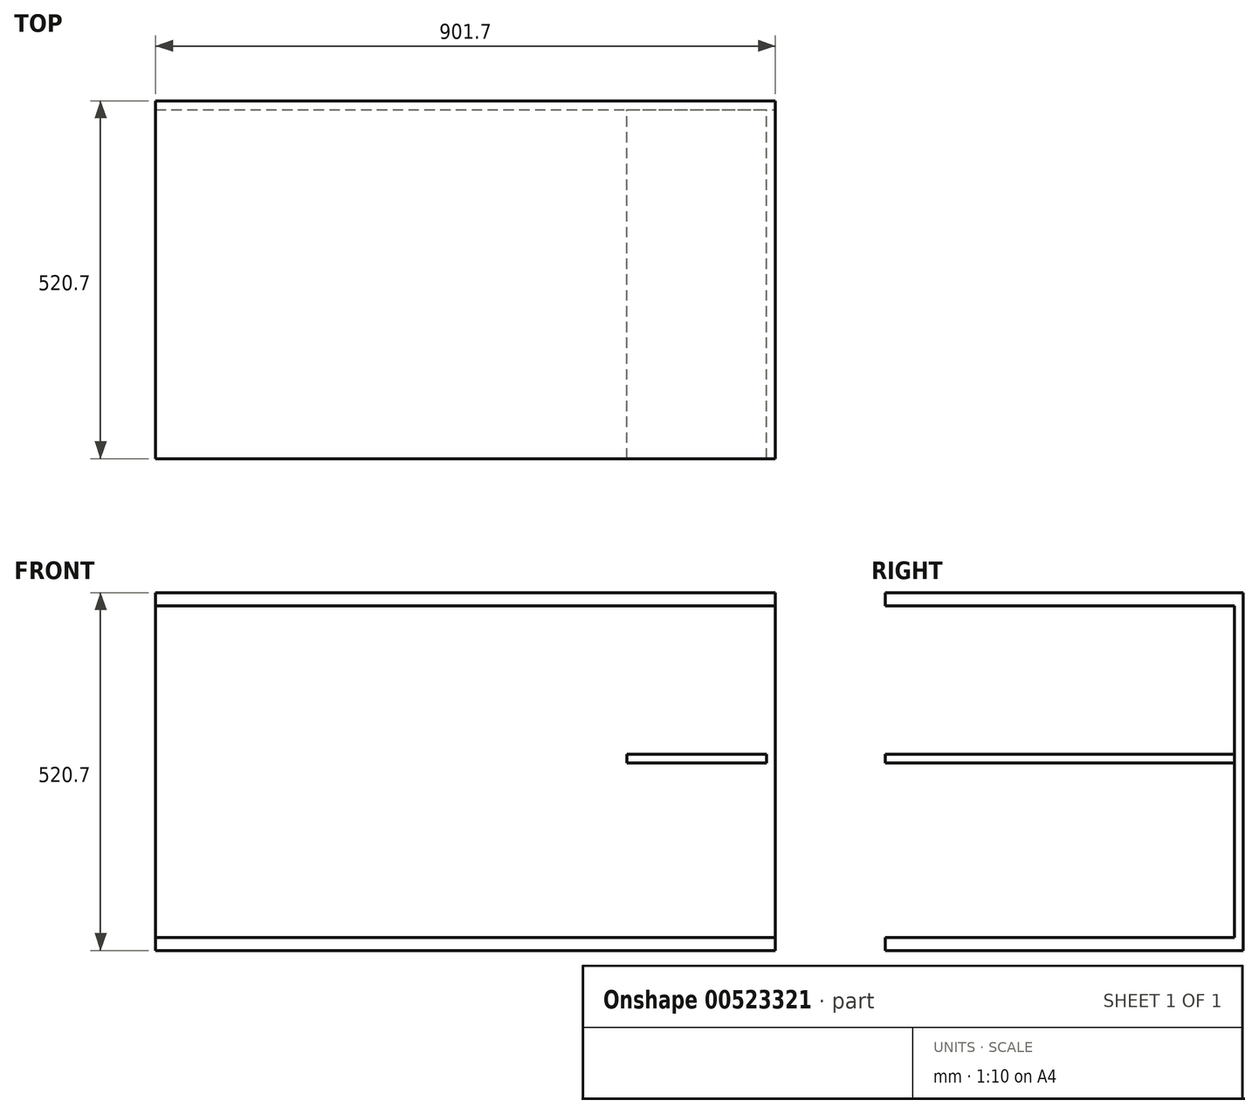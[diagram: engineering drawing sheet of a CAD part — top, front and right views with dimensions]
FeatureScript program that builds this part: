
annotation { "Feature Type Name" : "Feature", "Feature Type Description" : "" }
export const myFeature = defineFeature(function(context is Context, id is Id, definition is map)
    precondition{}
    {
        {
            var Q0;
            Q0=qCreatedBy(makeId("Front.planeOp"),FACE);
            var sketch = newSketch(context, id + "F0", { "sketchPlane" : qUnion([Q0])});
            skLineSegment(sketch, "E0.bottom", {"start": v(-12.7, 82.55) * mm, "end": v(889, 82.55) * mm});
            skLineSegment(sketch, "E0.top", {"start": v(-12.7, 63.5) * mm, "end": v(889, 63.5) * mm});
            skLineSegment(sketch, "E0.left", {"start": v(-12.7, 82.55) * mm, "end": v(-12.7, 63.5) * mm});
            skLineSegment(sketch, "E0.right", {"start": v(889, 82.55) * mm, "end": v(889, 63.5) * mm});
            skLineSegment(sketch, "E1.bottom", {"start": v(-12.7, 82.55) * mm, "end": v(0, 82.55) * mm});
            skLineSegment(sketch, "E1.top", {"start": v(-12.7, 565.15) * mm, "end": v(0, 565.15) * mm});
            skLineSegment(sketch, "E1.left", {"start": v(-12.7, 82.55) * mm, "end": v(-12.7, 565.15) * mm});
            skLineSegment(sketch, "E1.right", {"start": v(0, 82.55) * mm, "end": v(0, 565.15) * mm});
            skLineSegment(sketch, "E2.bottom", {"start": v(-12.7, 565.15) * mm, "end": v(889, 565.15) * mm});
            skLineSegment(sketch, "E2.top", {"start": v(-12.7, 584.2) * mm, "end": v(889, 584.2) * mm});
            skLineSegment(sketch, "E2.left", {"start": v(-12.7, 565.15) * mm, "end": v(-12.7, 584.2) * mm});
            skLineSegment(sketch, "E2.right", {"start": v(889, 565.15) * mm, "end": v(889, 584.2) * mm});
            skLineSegment(sketch, "E3.bottom", {"start": v(889, 82.55) * mm, "end": v(876.3, 82.55) * mm});
            skLineSegment(sketch, "E3.top", {"start": v(889, 565.15) * mm, "end": v(876.3, 565.15) * mm});
            skLineSegment(sketch, "E3.left", {"start": v(889, 82.55) * mm, "end": v(889, 565.15) * mm});
            skLineSegment(sketch, "E3.right", {"start": v(876.3, 82.55) * mm, "end": v(876.3, 565.15) * mm});
            skLineSegment(sketch, "E4.bottom", {"start": v(133.35, 400.05) * mm, "end": v(146.05, 400.05) * mm});
            skLineSegment(sketch, "E4.top", {"start": v(133.35, 82.55) * mm, "end": v(146.05, 82.55) * mm});
            skLineSegment(sketch, "E4.left", {"start": v(133.35, 400.05) * mm, "end": v(133.35, 82.55) * mm});
            skLineSegment(sketch, "E4.right", {"start": v(146.05, 400.05) * mm, "end": v(146.05, 82.55) * mm});
            skLineSegment(sketch, "E5.bottom", {"start": v(241.3, 400.05) * mm, "end": v(254, 400.05) * mm});
            skLineSegment(sketch, "E5.top", {"start": v(241.3, 82.55) * mm, "end": v(254, 82.55) * mm});
            skLineSegment(sketch, "E5.left", {"start": v(241.3, 400.05) * mm, "end": v(241.3, 82.55) * mm});
            skLineSegment(sketch, "E5.right", {"start": v(254, 400.05) * mm, "end": v(254, 82.55) * mm});
            skLineSegment(sketch, "E6.bottom", {"start": v(412.75, 400.05) * mm, "end": v(425.45, 400.05) * mm});
            skLineSegment(sketch, "E6.top", {"start": v(412.75, 82.55) * mm, "end": v(425.45, 82.55) * mm});
            skLineSegment(sketch, "E6.left", {"start": v(412.75, 400.05) * mm, "end": v(412.75, 82.55) * mm});
            skLineSegment(sketch, "E6.right", {"start": v(425.45, 400.05) * mm, "end": v(425.45, 82.55) * mm});
            skLineSegment(sketch, "E7.bottom", {"start": v(539.75, 400.05) * mm, "end": v(552.45, 400.05) * mm});
            skLineSegment(sketch, "E7.top", {"start": v(539.75, 82.55) * mm, "end": v(552.45, 82.55) * mm});
            skLineSegment(sketch, "E7.left", {"start": v(539.75, 400.05) * mm, "end": v(539.75, 82.55) * mm});
            skLineSegment(sketch, "E7.right", {"start": v(552.45, 400.05) * mm, "end": v(552.45, 82.55) * mm});
            skLineSegment(sketch, "E8.bottom", {"start": v(660.4, 82.55) * mm, "end": v(673.1, 82.55) * mm});
            skLineSegment(sketch, "E8.top", {"start": v(660.4, 400.05) * mm, "end": v(673.1, 400.05) * mm});
            skLineSegment(sketch, "E8.left", {"start": v(660.4, 82.55) * mm, "end": v(660.4, 400.05) * mm});
            skLineSegment(sketch, "E8.right", {"start": v(673.1, 82.55) * mm, "end": v(673.1, 400.05) * mm});
            skLineSegment(sketch, "E9.bottom", {"start": v(0, 400.05) * mm, "end": v(673.1, 400.05) * mm});
            skLineSegment(sketch, "E9.top", {"start": v(0, 412.75) * mm, "end": v(673.1, 412.75) * mm});
            skLineSegment(sketch, "E9.left", {"start": v(0, 400.05) * mm, "end": v(0, 412.75) * mm});
            skLineSegment(sketch, "E9.right", {"start": v(673.1, 400.05) * mm, "end": v(673.1, 412.75) * mm});
            skLineSegment(sketch, "E10.bottom", {"start": v(673.1, 349.25) * mm, "end": v(876.3, 349.25) * mm});
            skLineSegment(sketch, "E10.top", {"start": v(673.1, 336.55) * mm, "end": v(876.3, 336.55) * mm});
            skLineSegment(sketch, "E10.left", {"start": v(673.1, 349.25) * mm, "end": v(673.1, 336.55) * mm});
            skLineSegment(sketch, "E10.right", {"start": v(876.3, 349.25) * mm, "end": v(876.3, 336.55) * mm});
            skLineSegment(sketch, "E11.bottom", {"start": v(673.1, 412.75) * mm, "end": v(660.4, 412.75) * mm});
            skLineSegment(sketch, "E11.top", {"start": v(673.1, 565.15) * mm, "end": v(660.4, 565.15) * mm});
            skLineSegment(sketch, "E11.left", {"start": v(673.1, 412.75) * mm, "end": v(673.1, 565.15) * mm});
            skLineSegment(sketch, "E11.right", {"start": v(660.4, 412.75) * mm, "end": v(660.4, 565.15) * mm});
            skLineSegment(sketch, "E12.bottom", {"start": v(457.2, 565.15) * mm, "end": v(469.9, 565.15) * mm});
            skLineSegment(sketch, "E12.top", {"start": v(457.2, 412.75) * mm, "end": v(469.9, 412.75) * mm});
            skLineSegment(sketch, "E12.left", {"start": v(457.2, 565.15) * mm, "end": v(457.2, 412.75) * mm});
            skLineSegment(sketch, "E12.right", {"start": v(469.9, 565.15) * mm, "end": v(469.9, 412.75) * mm});
            skLineSegment(sketch, "E13.bottom", {"start": v(241.3, 565.15) * mm, "end": v(254, 565.15) * mm});
            skLineSegment(sketch, "E13.top", {"start": v(241.3, 412.75) * mm, "end": v(254, 412.75) * mm});
            skLineSegment(sketch, "E13.left", {"start": v(241.3, 565.15) * mm, "end": v(241.3, 412.75) * mm});
            skLineSegment(sketch, "E13.right", {"start": v(254, 565.15) * mm, "end": v(254, 412.75) * mm});
            skSolve(sketch);
        }
        {
            var Q0;
            Q0=makeQuery(id+"F0.imprint","IMPRINT",FACE,{"disambiguationData":[TD([[makeQuery(id+"F0.imprint","IMPRINT",EDGE,{"derivedFrom":sQuery(id+"F0.wireOp",EDGE,"E2.top")}),-1.0]])]});
            var Q1;
            Q1=makeQuery(id+"F0.imprint","IMPRINT",FACE,{"disambiguationData":[TD([[makeQuery(id+"F0.imprint","IMPRINT",EDGE,{"derivedFrom":sQuery(id+"F0.wireOp",EDGE,"E13.bottom")}),-1.0]])]});
            var Q2;
            {var subQ4=sQuery(id+"F0.wireOp",EDGE,"E1.bottom");Q2=makeQuery(id+"F0.imprint","IMPRINT",FACE,{"disambiguationData":[TD([[makeQuery(id+"F0.imprint","IMPRINT",EDGE,{"derivedFrom":subQ4}),1.0]])]});}
            var Q3;
            {var subQ10=sQuery(id+"F0.wireOp",EDGE,"E9.left");Q3=makeQuery(id+"F0.imprint","IMPRINT",FACE,{"disambiguationData":[TD([[makeQuery(id+"F0.imprint","IMPRINT",EDGE,{"derivedFrom":subQ10}),-1.0]])]});}
            var Q4;
            Q4=makeQuery(id+"F0.imprint","IMPRINT",FACE,{"disambiguationData":[TD([[makeQuery(id+"F0.imprint","IMPRINT",EDGE,{"derivedFrom":sQuery(id+"F0.wireOp",EDGE,"E4.top")}),1.0]])]});
            var Q5;
            Q5=makeQuery(id+"F0.imprint","IMPRINT",FACE,{"disambiguationData":[TD([[makeQuery(id+"F0.imprint","IMPRINT",EDGE,{"derivedFrom":sQuery(id+"F0.wireOp",EDGE,"E5.top")}),1.0]])]});
            var Q6;
            Q6=makeQuery(id+"F0.imprint","IMPRINT",FACE,{"disambiguationData":[TD([[makeQuery(id+"F0.imprint","IMPRINT",EDGE,{"derivedFrom":sQuery(id+"F0.wireOp",EDGE,"E0.top")}),1.0]])]});
            var Q7;
            Q7=makeQuery(id+"F0.imprint","IMPRINT",FACE,{"disambiguationData":[TD([[makeQuery(id+"F0.imprint","IMPRINT",EDGE,{"derivedFrom":sQuery(id+"F0.wireOp",EDGE,"E6.top")}),1.0]])]});
            var Q8;
            Q8=makeQuery(id+"F0.imprint","IMPRINT",FACE,{"disambiguationData":[TD([[makeQuery(id+"F0.imprint","IMPRINT",EDGE,{"derivedFrom":sQuery(id+"F0.wireOp",EDGE,"E12.bottom")}),-1.0]])]});
            var Q9;
            Q9=makeQuery(id+"F0.imprint","IMPRINT",FACE,{"disambiguationData":[TD([[makeQuery(id+"F0.imprint","IMPRINT",EDGE,{"derivedFrom":sQuery(id+"F0.wireOp",EDGE,"E7.top")}),1.0]])]});
            var Q10;
            {var subQ4=sQuery(id+"F0.wireOp",EDGE,"E8.bottom");Q10=makeQuery(id+"F0.imprint","IMPRINT",FACE,{"disambiguationData":[TD([[makeQuery(id+"F0.imprint","IMPRINT",EDGE,{"derivedFrom":subQ4}),1.0]])]});}
            var Q11;
            Q11=makeQuery(id+"F0.imprint","IMPRINT",FACE,{"disambiguationData":[TD([[makeQuery(id+"F0.imprint","IMPRINT",EDGE,{"derivedFrom":sQuery(id+"F0.wireOp",EDGE,"E10.bottom")}),-1.0]])]});
            var Q12;
            {var subQ1=sQuery(id+"F0.wireOp",EDGE,"E3.bottom");Q12=makeQuery(id+"F0.imprint","IMPRINT",FACE,{"disambiguationData":[TD([[makeQuery(id+"F0.imprint","IMPRINT",EDGE,{"derivedFrom":subQ1}),-1.0]])]});}
            var Q13;
            Q13=makeQuery(id+"F0.imprint","IMPRINT",FACE,{"disambiguationData":[TD([[makeQuery(id+"F0.imprint","IMPRINT",EDGE,{"derivedFrom":sQuery(id+"F0.wireOp",EDGE,"E11.bottom")}),-1.0]])]});
            extrude(context, id + "F1", {"entities" : qUnion([Q0, Q1, Q2, Q3, Q4, Q5, Q6, Q7, Q8, Q9, Q10, Q11, Q12, Q13]), "depth" : 508 * mm, "offsetDistance" : 25.4 * mm});
        }
        {
            var Q0;
            Q0=makeQuery(id+"F1.opExtrude","CAP_FACE",FACE,{"disambiguationData":[OSD([sQuery(id+"F0.wireOp",EDGE,"E0.bottom"),sQuery(id+"F0.wireOp",EDGE,"E0.top"),sQuery(id+"F0.wireOp",EDGE,"E0.left"),sQuery(id+"F0.wireOp",EDGE,"E0.right"),sQuery(id+"F0.wireOp",EDGE,"E1.left"),sQuery(id+"F0.wireOp",EDGE,"E1.right"),sQuery(id+"F0.wireOp",EDGE,"E2.bottom"),sQuery(id+"F0.wireOp",EDGE,"E2.top"),sQuery(id+"F0.wireOp",EDGE,"E2.left"),sQuery(id+"F0.wireOp",EDGE,"E2.right"),sQuery(id+"F0.wireOp",EDGE,"E3.left"),sQuery(id+"F0.wireOp",EDGE,"E3.right"),sQuery(id+"F0.wireOp",EDGE,"E4.left"),sQuery(id+"F0.wireOp",EDGE,"E4.right"),sQuery(id+"F0.wireOp",EDGE,"E5.left"),sQuery(id+"F0.wireOp",EDGE,"E5.right"),sQuery(id+"F0.wireOp",EDGE,"E6.left"),sQuery(id+"F0.wireOp",EDGE,"E6.right"),sQuery(id+"F0.wireOp",EDGE,"E7.left"),sQuery(id+"F0.wireOp",EDGE,"E7.right"),sQuery(id+"F0.wireOp",EDGE,"E8.left"),sQuery(id+"F0.wireOp",EDGE,"E8.right"),sQuery(id+"F0.wireOp",EDGE,"E9.bottom"),sQuery(id+"F0.wireOp",EDGE,"E9.top"),sQuery(id+"F0.wireOp",EDGE,"E9.right"),sQuery(id+"F0.wireOp",EDGE,"E10.bottom"),sQuery(id+"F0.wireOp",EDGE,"E10.top"),sQuery(id+"F0.wireOp",EDGE,"E11.left"),sQuery(id+"F0.wireOp",EDGE,"E11.right"),sQuery(id+"F0.wireOp",EDGE,"E12.left"),sQuery(id+"F0.wireOp",EDGE,"E12.right"),sQuery(id+"F0.wireOp",EDGE,"E13.left"),sQuery(id+"F0.wireOp",EDGE,"E13.right")])],"isStart":true});
            var sketch = newSketch(context, id + "F2", { "sketchPlane" : qUnion([Q0])});
            skLineSegment(sketch, "E14.bottom", {"start": v(-889, 584.2) * mm, "end": v(12.7, 584.2) * mm});
            skLineSegment(sketch, "E14.top", {"start": v(-889, 63.5) * mm, "end": v(12.7, 63.5) * mm});
            skLineSegment(sketch, "E14.left", {"start": v(-889, 584.2) * mm, "end": v(-889, 63.5) * mm});
            skLineSegment(sketch, "E14.right", {"start": v(12.7, 584.2) * mm, "end": v(12.7, 63.5) * mm});
            skSolve(sketch);
        }
        {
            var Q0;
            Q0 = qSketchRegion(id + "F2", true);
            extrude(context, id + "F3", {"entities" : qUnion([Q0]), "operationType" : NewBodyOperationType.ADD, "depth" : 12.7 * mm, "offsetDistance" : 25.4 * mm});
        }
    });
